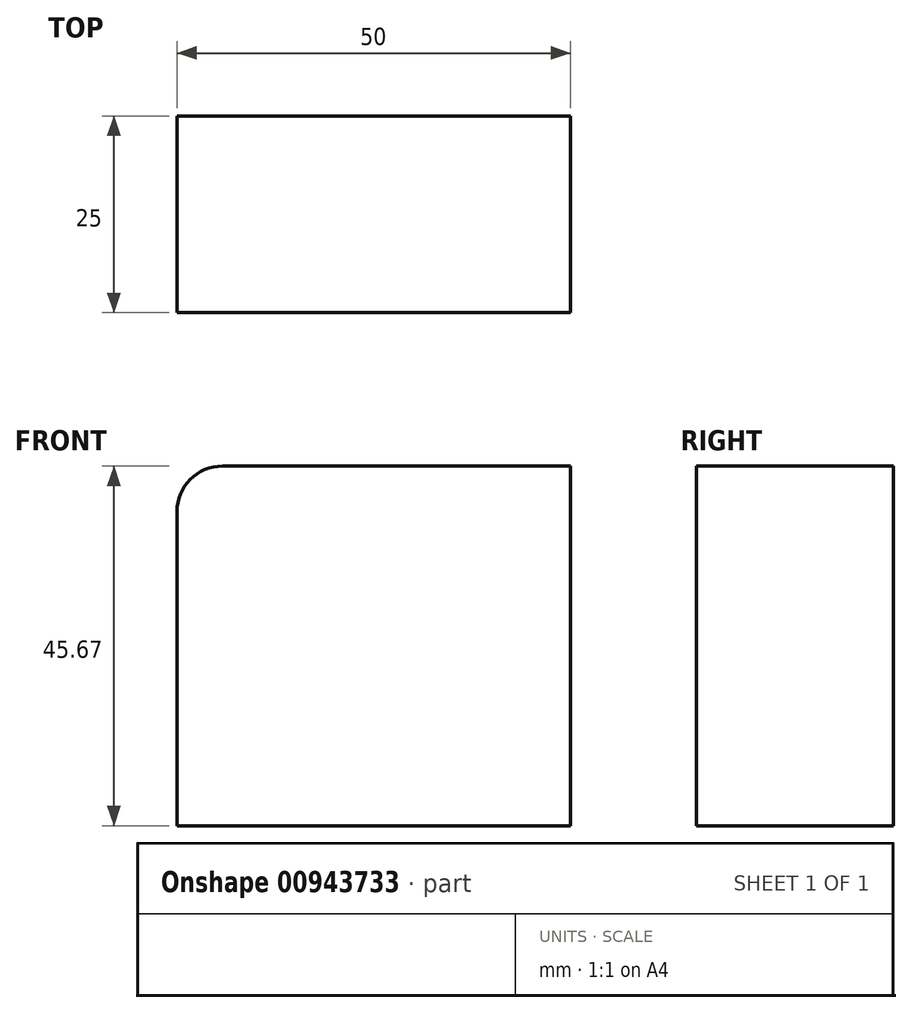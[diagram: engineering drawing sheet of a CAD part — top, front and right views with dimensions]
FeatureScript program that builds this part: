
annotation { "Feature Type Name" : "Feature", "Feature Type Description" : "" }
export const myFeature = defineFeature(function(context is Context, id is Id, definition is map)
    precondition{}
    {
        {
            var Q0;
            Q0=qCreatedBy(makeId("Front.planeOp"),FACE);
            var sketch = newSketch(context, id + "F0", { "sketchPlane" : qUnion([Q0])});
            skLineSegment(sketch, "E0.bottom", {"start": v(-285.48, 167.96) * mm, "end": v(-335.48, 167.96) * mm});
            skLineSegment(sketch, "E0.top", {"start": v(-285.48, 213.63) * mm, "end": v(-329.68, 213.63) * mm});
            skLineSegment(sketch, "E0.left", {"start": v(-285.48, 167.96) * mm, "end": v(-285.48, 213.63) * mm});
            skLineSegment(sketch, "E0.right", {"start": v(-335.48, 167.96) * mm, "end": v(-335.48, 207.83) * mm});
            skPoint(sketch, "E0.middle", {"position": v(-310.48, 190.8) * mm});
            skPoint(sketch, "E1.visualSharp", {"position": v(-335.48, 213.63) * mm});
            skArc(sketch, "E1.filletArc", {"start": v(-329.68, 213.63) * mm, "mid": v(-333.78, 211.94) * mm, "end": v(-335.48, 207.83) * mm});
            skSolve(sketch);
        }
        {
            var Q0;
            Q0 = qSketchRegion(id + "F0", true);
            extrude(context, id + "F1", {"entities" : qUnion([Q0]), "depth" : 25 * mm, "offsetDistance" : 25 * mm});
        }
    });
